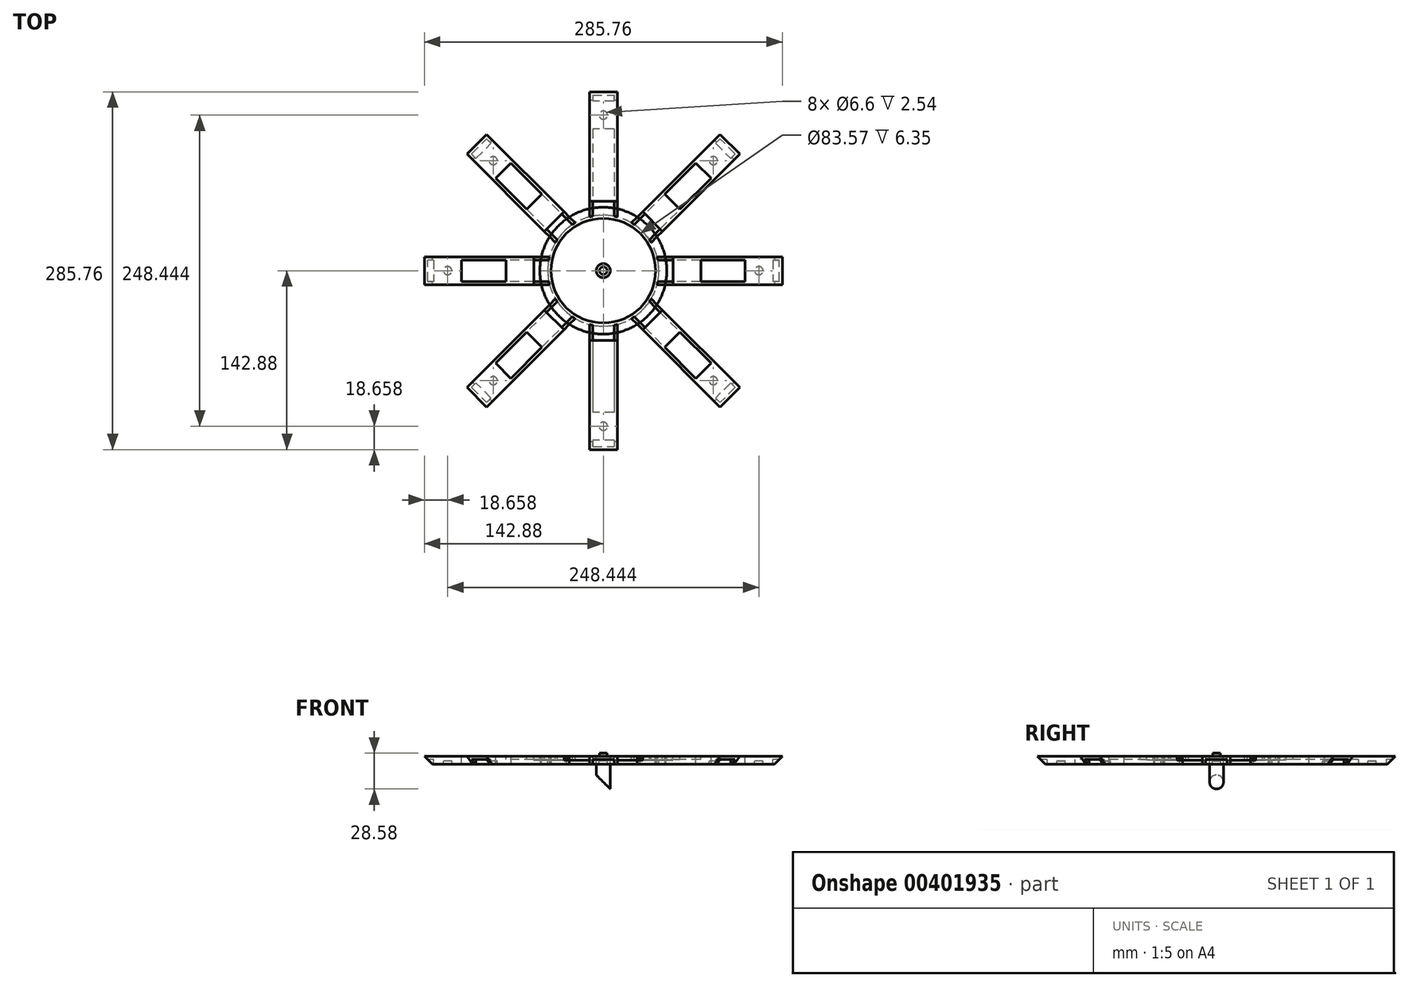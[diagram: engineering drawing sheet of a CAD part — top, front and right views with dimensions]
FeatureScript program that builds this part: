
annotation { "Feature Type Name" : "Feature", "Feature Type Description" : "" }
export const myFeature = defineFeature(function(context is Context, id is Id, definition is map)
    precondition{}
    {
        {
            var Q0;
            Q0=qCreatedBy(makeId("Top.planeOp"),FACE);
            var sketch = newSketch(context, id + "F0", { "sketchPlane" : qUnion([Q0])});
            skCircle(sketch, "E0", {"center": v(0, 0) * mm, "radius": 41.28 * mm, "construction": true});
            skLineSegment(sketch, "E1", {"start": v(0, 0) * mm, "end": v(142.88, 0) * mm, "construction": true});
            skLineSegment(sketch, "E2", {"start": v(0, 0) * mm, "end": v(0, 142.88) * mm, "construction": true});
            skLineSegment(sketch, "E3", {"start": v(0, 0) * mm, "end": v(-142.88, 0) * mm, "construction": true});
            skLineSegment(sketch, "E4", {"start": v(0, 0) * mm, "end": v(0, -142.88) * mm, "construction": true});
            skLineSegment(sketch, "E5", {"start": v(0, 0) * mm, "end": v(101.03, 101.03) * mm, "construction": true});
            skLineSegment(sketch, "E6", {"start": v(0, 0) * mm, "end": v(101.03, -101.03) * mm, "construction": true});
            skLineSegment(sketch, "E7", {"start": v(0, 0) * mm, "end": v(-101.03, -101.03) * mm, "construction": true});
            skLineSegment(sketch, "E8", {"start": v(0, 0) * mm, "end": v(-101.03, 101.03) * mm, "construction": true});
            skLineSegment(sketch, "E9.bottom", {"start": v(-11.11, 142.88) * mm, "end": v(11.11, 142.88) * mm});
            skLineSegment(sketch, "E9.top", {"start": v(-11.11, -142.88) * mm, "end": v(11.11, -142.88) * mm});
            skLineSegment(sketch, "E9.left", {"start": v(-11.11, 142.88) * mm, "end": v(-11.11, -142.88) * mm});
            skLineSegment(sketch, "E9.right", {"start": v(11.11, 142.88) * mm, "end": v(11.11, -142.88) * mm});
            skLineSegment(sketch, "E10.bottom", {"start": v(142.88, -11.11) * mm, "end": v(-142.88, -11.11) * mm});
            skLineSegment(sketch, "E10.top", {"start": v(142.88, 11.11) * mm, "end": v(-142.88, 11.11) * mm});
            skLineSegment(sketch, "E10.left", {"start": v(142.88, -11.11) * mm, "end": v(142.88, 11.11) * mm});
            skLineSegment(sketch, "E10.right", {"start": v(-142.88, -11.11) * mm, "end": v(-142.88, 11.11) * mm});
            skLineSegment(sketch, "E11", {"start": v(-108.89, 93.17) * mm, "end": v(93.17, -108.89) * mm});
            skLineSegment(sketch, "E12", {"start": v(-93.17, 108.89) * mm, "end": v(108.89, -93.17) * mm});
            skLineSegment(sketch, "E13", {"start": v(108.89, -93.17) * mm, "end": v(93.17, -108.89) * mm});
            skLineSegment(sketch, "E14", {"start": v(-108.89, 93.17) * mm, "end": v(-93.17, 108.89) * mm});
            skLineSegment(sketch, "E15", {"start": v(-108.89, -93.17) * mm, "end": v(-93.17, -108.89) * mm});
            skLineSegment(sketch, "E16", {"start": v(-93.17, -108.89) * mm, "end": v(108.89, 93.17) * mm});
            skLineSegment(sketch, "E17", {"start": v(108.89, 93.17) * mm, "end": v(93.17, 108.89) * mm});
            skLineSegment(sketch, "E18", {"start": v(93.17, 108.89) * mm, "end": v(-108.89, -93.17) * mm});
            skLineSegment(sketch, "E19", {"start": v(-120.65, 11.11) * mm, "end": v(-120.65, -11.11) * mm});
            skLineSegment(sketch, "E20", {"start": v(-93.17, 77.45) * mm, "end": v(-77.45, 93.17) * mm});
            skLineSegment(sketch, "E21", {"start": v(-11.11, 120.65) * mm, "end": v(11.11, 120.65) * mm});
            skLineSegment(sketch, "E22", {"start": v(77.45, 93.17) * mm, "end": v(93.17, 77.45) * mm});
            skLineSegment(sketch, "E23", {"start": v(120.65, 11.11) * mm, "end": v(120.65, -11.11) * mm});
            skLineSegment(sketch, "E24", {"start": v(11.11, -120.65) * mm, "end": v(-11.11, -120.65) * mm});
            skLineSegment(sketch, "E25", {"start": v(-93.17, -77.45) * mm, "end": v(-77.45, -93.17) * mm});
            skLineSegment(sketch, "E26", {"start": v(77.45, -93.17) * mm, "end": v(93.17, -77.45) * mm});
            skSolve(sketch);
        }
        {
            var Q0;
            Q0 = qSketchRegion(id + "F0", true);
            extrude(context, id + "F1", {"entities" : qUnion([Q0]), "oppositeDirection" : true, "depth" : 6.35 * mm});
        }
        {
            var Q0;
            Q0=makeQuery(id+"F1.opExtrude","CAP_FACE",FACE,{"disambiguationData":[OSD([sQuery(id+"F0.wireOp",EDGE,"E9.bottom"),sQuery(id+"F0.wireOp",EDGE,"E9.top"),sQuery(id+"F0.wireOp",EDGE,"E9.left"),sQuery(id+"F0.wireOp",EDGE,"E9.right"),sQuery(id+"F0.wireOp",EDGE,"E10.bottom"),sQuery(id+"F0.wireOp",EDGE,"E10.top"),sQuery(id+"F0.wireOp",EDGE,"E10.left"),sQuery(id+"F0.wireOp",EDGE,"E10.right"),sQuery(id+"F0.wireOp",EDGE,"E11"),sQuery(id+"F0.wireOp",EDGE,"E12"),sQuery(id+"F0.wireOp",EDGE,"E13"),sQuery(id+"F0.wireOp",EDGE,"E14"),sQuery(id+"F0.wireOp",EDGE,"E15"),sQuery(id+"F0.wireOp",EDGE,"E16"),sQuery(id+"F0.wireOp",EDGE,"E17"),sQuery(id+"F0.wireOp",EDGE,"E18")])],"isStart":false});
            shell(context, id + "F2", {"entities" : qUnion([Q0]), "thickness" : 2.54 * mm});
        }
        {
            var Q0;
            Q0=makeQuery(id+"F1.opExtrude","CAP_EDGE",EDGE,{"disambiguationData":[OSD([sQuery(id+"F0.wireOp",EDGE,"E15")])],"isStart":false});
            var Q1;
            Q1=makeQuery(id+"F1.opExtrude","CAP_EDGE",EDGE,{"disambiguationData":[OSD([sQuery(id+"F0.wireOp",EDGE,"E10.right")])],"isStart":false});
            var Q2;
            Q2=makeQuery(id+"F1.opExtrude","CAP_EDGE",EDGE,{"disambiguationData":[OSD([sQuery(id+"F0.wireOp",EDGE,"E14")])],"isStart":false});
            var Q3;
            Q3=makeQuery(id+"F1.opExtrude","CAP_EDGE",EDGE,{"disambiguationData":[OSD([sQuery(id+"F0.wireOp",EDGE,"E9.bottom")])],"isStart":false});
            var Q4;
            Q4=makeQuery(id+"F1.opExtrude","CAP_EDGE",EDGE,{"disambiguationData":[OSD([sQuery(id+"F0.wireOp",EDGE,"E17")])],"isStart":false});
            var Q5;
            Q5=makeQuery(id+"F1.opExtrude","CAP_EDGE",EDGE,{"disambiguationData":[OSD([sQuery(id+"F0.wireOp",EDGE,"E10.left")])],"isStart":false});
            var Q6;
            Q6=makeQuery(id+"F1.opExtrude","CAP_EDGE",EDGE,{"disambiguationData":[OSD([sQuery(id+"F0.wireOp",EDGE,"E13")])],"isStart":false});
            var Q7;
            Q7=makeQuery(id+"F1.opExtrude","CAP_EDGE",EDGE,{"disambiguationData":[OSD([sQuery(id+"F0.wireOp",EDGE,"E9.top")])],"isStart":false});
            chamfer(context, id + "F3", {"entities" : qUnion([Q0, Q1, Q2, Q3, Q4, Q5, Q6, Q7]), "width" : 6.35 * mm, "tangentPropagation" : true});
        }
        {
            var Q0;
            Q0=qCreatedBy(makeId("Top.planeOp"),FACE);
            var sketch = newSketch(context, id + "F4", { "sketchPlane" : qUnion([Q0])});
            skLineSegment(sketch, "E27", {"start": v(0, 0) * mm, "end": v(142.88, 0) * mm, "construction": true});
            skLineSegment(sketch, "E28", {"start": v(0, 0) * mm, "end": v(101.03, -101.03) * mm, "construction": true});
            skLineSegment(sketch, "E29", {"start": v(0, 0) * mm, "end": v(0, 142.88) * mm, "construction": true});
            skLineSegment(sketch, "E30", {"start": v(0, 0) * mm, "end": v(101.03, 101.03) * mm, "construction": true});
            skLineSegment(sketch, "E31", {"start": v(0, 0) * mm, "end": v(-101.03, 101.03) * mm, "construction": true});
            skLineSegment(sketch, "E32", {"start": v(0, 0) * mm, "end": v(-101.03, -101.03) * mm, "construction": true});
            skLineSegment(sketch, "E33", {"start": v(0, 0) * mm, "end": v(-142.88, 0) * mm, "construction": true});
            skLineSegment(sketch, "E34", {"start": v(0, 0) * mm, "end": v(0, -142.88) * mm, "construction": true});
            skLineSegment(sketch, "E35", {"start": v(-142.88, 11.11) * mm, "end": v(-142.88, -11.11) * mm});
            skLineSegment(sketch, "E36", {"start": v(-142.88, -11.11) * mm, "end": v(-120.65, -11.11) * mm});
            skLineSegment(sketch, "E37", {"start": v(-120.65, -11.11) * mm, "end": v(-120.65, 11.11) * mm});
            skLineSegment(sketch, "E38", {"start": v(-120.65, 11.11) * mm, "end": v(-142.88, 11.11) * mm});
            skLineSegment(sketch, "E39", {"start": v(142.88, 11.11) * mm, "end": v(142.88, -11.11) * mm});
            skLineSegment(sketch, "E40", {"start": v(142.88, -11.11) * mm, "end": v(120.65, -11.11) * mm});
            skLineSegment(sketch, "E41", {"start": v(120.65, -11.11) * mm, "end": v(120.65, 11.11) * mm});
            skLineSegment(sketch, "E42", {"start": v(120.65, 11.11) * mm, "end": v(142.88, 11.11) * mm});
            skLineSegment(sketch, "E43", {"start": v(11.11, 142.88) * mm, "end": v(-11.11, 142.88) * mm});
            skLineSegment(sketch, "E44", {"start": v(-11.11, 142.88) * mm, "end": v(-11.11, 120.65) * mm});
            skLineSegment(sketch, "E45", {"start": v(-11.11, 120.65) * mm, "end": v(11.11, 120.65) * mm});
            skLineSegment(sketch, "E46", {"start": v(11.11, 120.65) * mm, "end": v(11.11, 142.88) * mm});
            skLineSegment(sketch, "E47", {"start": v(11.11, -142.88) * mm, "end": v(-11.11, -142.88) * mm});
            skLineSegment(sketch, "E48", {"start": v(-11.11, -142.88) * mm, "end": v(-11.11, -120.65) * mm});
            skLineSegment(sketch, "E49", {"start": v(-11.11, -120.65) * mm, "end": v(11.11, -120.65) * mm});
            skLineSegment(sketch, "E50", {"start": v(11.11, -120.65) * mm, "end": v(11.11, -142.88) * mm});
            skLineSegment(sketch, "E51", {"start": v(-101.03, 101.03) * mm, "end": v(-93.17, 108.89) * mm});
            skLineSegment(sketch, "E52", {"start": v(-93.17, 108.89) * mm, "end": v(-77.45, 93.17) * mm});
            skLineSegment(sketch, "E53", {"start": v(-77.45, 93.17) * mm, "end": v(-93.17, 77.45) * mm});
            skLineSegment(sketch, "E54", {"start": v(-93.17, 77.45) * mm, "end": v(-108.89, 93.17) * mm});
            skLineSegment(sketch, "E55", {"start": v(-108.89, 93.17) * mm, "end": v(-101.03, 101.03) * mm});
            skLineSegment(sketch, "E56", {"start": v(101.03, -101.03) * mm, "end": v(108.89, -93.17) * mm});
            skLineSegment(sketch, "E57", {"start": v(108.89, -93.17) * mm, "end": v(93.17, -77.45) * mm});
            skLineSegment(sketch, "E58", {"start": v(93.17, -77.45) * mm, "end": v(77.45, -93.17) * mm});
            skLineSegment(sketch, "E59", {"start": v(77.45, -93.17) * mm, "end": v(93.17, -108.89) * mm});
            skLineSegment(sketch, "E60", {"start": v(93.17, -108.89) * mm, "end": v(101.03, -101.03) * mm});
            skLineSegment(sketch, "E61", {"start": v(101.03, 101.03) * mm, "end": v(93.17, 108.89) * mm});
            skLineSegment(sketch, "E62", {"start": v(93.17, 108.89) * mm, "end": v(77.45, 93.17) * mm});
            skLineSegment(sketch, "E63", {"start": v(77.45, 93.17) * mm, "end": v(93.17, 77.45) * mm});
            skLineSegment(sketch, "E64", {"start": v(93.17, 77.45) * mm, "end": v(108.89, 93.17) * mm});
            skLineSegment(sketch, "E65", {"start": v(108.89, 93.17) * mm, "end": v(101.03, 101.03) * mm});
            skLineSegment(sketch, "E66", {"start": v(-101.03, -101.03) * mm, "end": v(-108.89, -93.17) * mm});
            skLineSegment(sketch, "E67", {"start": v(-108.89, -93.17) * mm, "end": v(-93.17, -77.45) * mm});
            skLineSegment(sketch, "E68", {"start": v(-93.17, -77.45) * mm, "end": v(-77.45, -93.17) * mm});
            skLineSegment(sketch, "E69", {"start": v(-77.45, -93.17) * mm, "end": v(-93.17, -108.89) * mm});
            skLineSegment(sketch, "E70", {"start": v(-93.17, -108.89) * mm, "end": v(-101.03, -101.03) * mm});
            skLineSegment(sketch, "E71", {"start": v(0, 0) * mm, "end": v(0, 77.79) * mm, "construction": true});
            skLineSegment(sketch, "E72", {"start": v(0, 0) * mm, "end": v(55, 55) * mm, "construction": true});
            skLineSegment(sketch, "E73", {"start": v(0, 0) * mm, "end": v(77.79, 0) * mm, "construction": true});
            skLineSegment(sketch, "E74", {"start": v(0, 0) * mm, "end": v(55, -55) * mm, "construction": true});
            skLineSegment(sketch, "E75", {"start": v(0, 0) * mm, "end": v(0, -77.79) * mm, "construction": true});
            skLineSegment(sketch, "E76", {"start": v(0, 0) * mm, "end": v(-55, -55) * mm, "construction": true});
            skLineSegment(sketch, "E77", {"start": v(0, 0) * mm, "end": v(-77.79, 0) * mm, "construction": true});
            skLineSegment(sketch, "E78", {"start": v(0, 0) * mm, "end": v(-55, 55) * mm, "construction": true});
            skLineSegment(sketch, "E79", {"start": v(77.79, 11.11) * mm, "end": v(77.79, -11.11) * mm});
            skLineSegment(sketch, "E80", {"start": v(77.79, -11.11) * mm, "end": v(55.56, -11.11) * mm});
            skLineSegment(sketch, "E81", {"start": v(55.56, -11.11) * mm, "end": v(55.56, 11.11) * mm});
            skLineSegment(sketch, "E82", {"start": v(55.56, 11.11) * mm, "end": v(77.79, 11.11) * mm});
            skLineSegment(sketch, "E83", {"start": v(55, -55) * mm, "end": v(47.15, -62.86) * mm});
            skLineSegment(sketch, "E84", {"start": v(47.15, -62.86) * mm, "end": v(31.43, -47.15) * mm});
            skLineSegment(sketch, "E85", {"start": v(31.43, -47.15) * mm, "end": v(47.15, -31.43) * mm});
            skLineSegment(sketch, "E86", {"start": v(47.15, -31.43) * mm, "end": v(62.86, -47.15) * mm});
            skLineSegment(sketch, "E87", {"start": v(62.86, -47.15) * mm, "end": v(55, -55) * mm});
            skLineSegment(sketch, "E88", {"start": v(11.11, -77.79) * mm, "end": v(-11.11, -77.79) * mm});
            skLineSegment(sketch, "E89", {"start": v(-11.11, -77.79) * mm, "end": v(-11.11, -55.56) * mm});
            skLineSegment(sketch, "E90", {"start": v(-11.11, -55.56) * mm, "end": v(11.11, -55.56) * mm});
            skLineSegment(sketch, "E91", {"start": v(11.11, -55.56) * mm, "end": v(11.11, -77.79) * mm});
            skLineSegment(sketch, "E92", {"start": v(-55, -55) * mm, "end": v(-62.86, -47.15) * mm});
            skLineSegment(sketch, "E93", {"start": v(-62.86, -47.15) * mm, "end": v(-47.15, -31.43) * mm});
            skLineSegment(sketch, "E94", {"start": v(-47.15, -31.43) * mm, "end": v(-31.43, -47.15) * mm});
            skLineSegment(sketch, "E95", {"start": v(-31.43, -47.15) * mm, "end": v(-47.15, -62.86) * mm});
            skLineSegment(sketch, "E96", {"start": v(-47.15, -62.86) * mm, "end": v(-55, -55) * mm});
            skLineSegment(sketch, "E97", {"start": v(-77.79, 11.11) * mm, "end": v(-77.79, -11.11) * mm});
            skLineSegment(sketch, "E98", {"start": v(-77.79, -11.11) * mm, "end": v(-55.56, -11.11) * mm});
            skLineSegment(sketch, "E99", {"start": v(-55.56, -11.11) * mm, "end": v(-55.56, 11.11) * mm});
            skLineSegment(sketch, "E100", {"start": v(-55.56, 11.11) * mm, "end": v(-77.79, 11.11) * mm});
            skLineSegment(sketch, "E101", {"start": v(-55, 55) * mm, "end": v(-47.15, 62.86) * mm});
            skLineSegment(sketch, "E102", {"start": v(-47.15, 62.86) * mm, "end": v(-31.43, 47.15) * mm});
            skLineSegment(sketch, "E103", {"start": v(-31.43, 47.15) * mm, "end": v(-47.15, 31.43) * mm});
            skLineSegment(sketch, "E104", {"start": v(-47.15, 31.43) * mm, "end": v(-62.86, 47.15) * mm});
            skLineSegment(sketch, "E105", {"start": v(-62.86, 47.15) * mm, "end": v(-55, 55) * mm});
            skLineSegment(sketch, "E106", {"start": v(-11.11, 77.79) * mm, "end": v(11.11, 77.79) * mm});
            skLineSegment(sketch, "E107", {"start": v(11.11, 77.79) * mm, "end": v(11.11, 55.56) * mm});
            skLineSegment(sketch, "E108", {"start": v(11.11, 55.56) * mm, "end": v(-11.11, 55.56) * mm});
            skLineSegment(sketch, "E109", {"start": v(-11.11, 55.56) * mm, "end": v(-11.11, 77.79) * mm});
            skLineSegment(sketch, "E110", {"start": v(55, 55) * mm, "end": v(62.86, 47.15) * mm});
            skLineSegment(sketch, "E111", {"start": v(62.86, 47.15) * mm, "end": v(47.15, 31.43) * mm});
            skLineSegment(sketch, "E112", {"start": v(47.15, 31.43) * mm, "end": v(31.43, 47.15) * mm});
            skLineSegment(sketch, "E113", {"start": v(31.43, 47.15) * mm, "end": v(47.15, 62.86) * mm});
            skLineSegment(sketch, "E114", {"start": v(47.15, 62.86) * mm, "end": v(55, 55) * mm});
            skLineSegment(sketch, "E115", {"start": v(0, 77.79) * mm, "end": v(0, 120.65) * mm, "construction": true});
            skLineSegment(sketch, "E116", {"start": v(55, 55) * mm, "end": v(85.31, 85.31) * mm, "construction": true});
            skLineSegment(sketch, "E117", {"start": v(77.79, 0) * mm, "end": v(120.65, 0) * mm, "construction": true});
            skLineSegment(sketch, "E118", {"start": v(55, -55) * mm, "end": v(85.31, -85.31) * mm, "construction": true});
            skLineSegment(sketch, "E119", {"start": v(0, -77.79) * mm, "end": v(0, -120.65) * mm, "construction": true});
            skLineSegment(sketch, "E120", {"start": v(-55, -55) * mm, "end": v(-85.31, -85.31) * mm, "construction": true});
            skLineSegment(sketch, "E121", {"start": v(-77.79, 0) * mm, "end": v(-120.65, 0) * mm, "construction": true});
            skLineSegment(sketch, "E122", {"start": v(-55, 55) * mm, "end": v(-85.31, 85.31) * mm, "construction": true});
            skLineSegment(sketch, "E123.bottom", {"start": v(8.57, 77.79) * mm, "end": v(-8.57, 77.79) * mm});
            skLineSegment(sketch, "E123.top", {"start": v(8.57, 120.65) * mm, "end": v(-8.57, 120.65) * mm});
            skLineSegment(sketch, "E123.left", {"start": v(8.57, 77.79) * mm, "end": v(8.57, 120.65) * mm});
            skLineSegment(sketch, "E123.right", {"start": v(-8.57, 77.79) * mm, "end": v(-8.57, 120.65) * mm});
            skPoint(sketch, "E123.middle", {"position": v(0, 99.22) * mm});
            skLineSegment(sketch, "E124.bottom", {"start": v(77.79, 8.57) * mm, "end": v(120.65, 8.57) * mm});
            skLineSegment(sketch, "E124.top", {"start": v(77.79, -8.57) * mm, "end": v(120.65, -8.57) * mm});
            skLineSegment(sketch, "E124.left", {"start": v(77.79, 8.57) * mm, "end": v(77.79, -8.57) * mm});
            skLineSegment(sketch, "E124.right", {"start": v(120.65, 8.57) * mm, "end": v(120.65, -8.57) * mm});
            skPoint(sketch, "E124.middle", {"position": v(99.22, 0) * mm});
            skLineSegment(sketch, "E125.bottom", {"start": v(8.57, -77.79) * mm, "end": v(-8.57, -77.79) * mm});
            skLineSegment(sketch, "E125.top", {"start": v(8.57, -120.65) * mm, "end": v(-8.57, -120.65) * mm});
            skLineSegment(sketch, "E125.left", {"start": v(8.57, -77.79) * mm, "end": v(8.57, -120.65) * mm});
            skLineSegment(sketch, "E125.right", {"start": v(-8.57, -77.79) * mm, "end": v(-8.57, -120.65) * mm});
            skPoint(sketch, "E125.middle", {"position": v(0, -99.22) * mm});
            skLineSegment(sketch, "E126.bottom", {"start": v(-77.79, -8.57) * mm, "end": v(-120.65, -8.57) * mm});
            skLineSegment(sketch, "E126.top", {"start": v(-77.79, 8.57) * mm, "end": v(-120.65, 8.57) * mm});
            skLineSegment(sketch, "E126.left", {"start": v(-77.79, -8.57) * mm, "end": v(-77.79, 8.57) * mm});
            skLineSegment(sketch, "E126.right", {"start": v(-120.65, -8.57) * mm, "end": v(-120.65, 8.57) * mm});
            skPoint(sketch, "E126.middle", {"position": v(-99.22, 0) * mm});
            skLineSegment(sketch, "E127", {"start": v(-79.25, 91.37) * mm, "end": v(-48.94, 61.07) * mm});
            skLineSegment(sketch, "E128", {"start": v(-91.37, 79.25) * mm, "end": v(-61.07, 48.94) * mm});
            skLineSegment(sketch, "E129", {"start": v(79.25, 91.37) * mm, "end": v(48.94, 61.07) * mm});
            skLineSegment(sketch, "E130", {"start": v(91.37, 79.25) * mm, "end": v(61.07, 48.94) * mm});
            skLineSegment(sketch, "E131", {"start": v(-91.37, -79.25) * mm, "end": v(-61.07, -48.94) * mm});
            skLineSegment(sketch, "E132", {"start": v(-79.25, -91.37) * mm, "end": v(-48.94, -61.07) * mm});
            skLineSegment(sketch, "E133", {"start": v(48.94, -61.07) * mm, "end": v(79.25, -91.37) * mm});
            skLineSegment(sketch, "E134", {"start": v(61.07, -48.94) * mm, "end": v(91.37, -79.25) * mm});
            skLineSegment(sketch, "E135", {"start": v(-77.79, 8.57) * mm, "end": v(77.79, 8.57) * mm});
            skLineSegment(sketch, "E136", {"start": v(-77.79, -8.57) * mm, "end": v(77.79, -8.57) * mm});
            skLineSegment(sketch, "E137", {"start": v(-8.57, 77.79) * mm, "end": v(-8.57, -77.79) * mm});
            skLineSegment(sketch, "E138", {"start": v(8.57, 77.79) * mm, "end": v(8.57, -77.79) * mm});
            skLineSegment(sketch, "E139", {"start": v(-61.07, 48.94) * mm, "end": v(48.94, -61.07) * mm});
            skLineSegment(sketch, "E140", {"start": v(-48.94, 61.07) * mm, "end": v(61.07, -48.94) * mm});
            skLineSegment(sketch, "E141", {"start": v(-61.07, -48.94) * mm, "end": v(48.94, 61.07) * mm});
            skLineSegment(sketch, "E142", {"start": v(-48.94, -61.07) * mm, "end": v(61.07, 48.94) * mm});
            skLineSegment(sketch, "E143", {"start": v(-31.43, 47.15) * mm, "end": v(47.15, -31.43) * mm});
            skLineSegment(sketch, "E144", {"start": v(-47.15, 31.43) * mm, "end": v(31.43, -47.15) * mm});
            skLineSegment(sketch, "E145", {"start": v(-11.11, 55.56) * mm, "end": v(-11.11, -55.56) * mm});
            skLineSegment(sketch, "E146", {"start": v(11.11, 55.56) * mm, "end": v(11.11, -55.56) * mm});
            skLineSegment(sketch, "E147", {"start": v(31.43, 47.15) * mm, "end": v(-47.15, -31.43) * mm});
            skLineSegment(sketch, "E148", {"start": v(-31.43, -47.15) * mm, "end": v(47.15, 31.43) * mm});
            skLineSegment(sketch, "E149", {"start": v(55.56, 11.11) * mm, "end": v(-55.56, 11.11) * mm});
            skLineSegment(sketch, "E150", {"start": v(-55.56, -11.11) * mm, "end": v(55.56, -11.11) * mm});
            skCircle(sketch, "E151", {"center": v(0, 0) * mm, "radius": 44.32 * mm});
            skSolve(sketch);
        }
        {
            var Q0;
            Q0=makeQuery(id+"F4.imprint","IMPRINT",FACE,{"disambiguationData":[TD([[makeQuery(id+"F4.imprint","IMPRINT",EDGE,{"derivedFrom":sQuery(id+"F4.wireOp",EDGE,"E126.bottom")}),-1.0]])]});
            var Q1;
            {var subQ4=sQuery(id+"F4.wireOp",EDGE,"E127");Q1=makeQuery(id+"F4.imprint","IMPRINT",FACE,{"disambiguationData":[TD([[makeQuery(id+"F4.imprint","IMPRINT",EDGE,{"derivedFrom":subQ4}),-1.0]])]});}
            var Q2;
            Q2=makeQuery(id+"F4.imprint","IMPRINT",FACE,{"disambiguationData":[TD([[makeQuery(id+"F4.imprint","IMPRINT",EDGE,{"derivedFrom":sQuery(id+"F4.wireOp",EDGE,"E123.bottom")}),-1.0]])]});
            var Q3;
            {var subQ0=sQuery(id+"F4.wireOp",EDGE,"E129");Q3=makeQuery(id+"F4.imprint","IMPRINT",FACE,{"disambiguationData":[TD([[makeQuery(id+"F4.imprint","IMPRINT",EDGE,{"derivedFrom":subQ0}),1.0]])]});}
            var Q4;
            Q4=makeQuery(id+"F4.imprint","IMPRINT",FACE,{"disambiguationData":[TD([[makeQuery(id+"F4.imprint","IMPRINT",EDGE,{"derivedFrom":sQuery(id+"F4.wireOp",EDGE,"E124.bottom")}),-1.0]])]});
            var Q5;
            {var subQ0=sQuery(id+"F4.wireOp",EDGE,"E133");Q5=makeQuery(id+"F4.imprint","IMPRINT",FACE,{"disambiguationData":[TD([[makeQuery(id+"F4.imprint","IMPRINT",EDGE,{"derivedFrom":subQ0}),1.0]])]});}
            var Q6;
            Q6=makeQuery(id+"F4.imprint","IMPRINT",FACE,{"disambiguationData":[TD([[makeQuery(id+"F4.imprint","IMPRINT",EDGE,{"derivedFrom":sQuery(id+"F4.wireOp",EDGE,"E125.bottom")}),1.0]])]});
            var Q7;
            {var subQ0=sQuery(id+"F4.wireOp",EDGE,"E131");Q7=makeQuery(id+"F4.imprint","IMPRINT",FACE,{"disambiguationData":[TD([[makeQuery(id+"F4.imprint","IMPRINT",EDGE,{"derivedFrom":subQ0}),-1.0]])]});}
            extrude(context, id + "F5", {"entities" : qUnion([Q0, Q1, Q2, Q3, Q4, Q5, Q6, Q7]), "operationType" : NewBodyOperationType.REMOVE, "oppositeDirection" : true, "depth" : 25.4 * mm});
        }
        {
            var Q0;
            {var subQ1=sQuery(id+"F4.wireOp",EDGE,"E103");var subQ7=sQuery(id+"F4.wireOp",EDGE,"E140");var subQ8=makeQuery(id+"F4.imprint","INTERSECT",VERTEX,{"derivedFrom":[subQ1,subQ7]});Q0=makeQuery(id+"F4.imprint","IMPRINT",FACE,{"disambiguationData":[TD([[makeQuery(id+"F4.imprint","IMPRINT",EDGE,{"disambiguationData":[TD([[subQ8,-1.0]])],"derivedFrom":subQ1}),1.0]])]});}
            var Q1;
            {var subQ0=sQuery(id+"F4.wireOp",EDGE,"E139");var subQ1=sQuery(id+"F4.wireOp",EDGE,"E135");var subQ2=makeQuery(id+"F4.imprint","INTERSECT",VERTEX,{"derivedFrom":[subQ1,subQ0]});Q1=makeQuery(id+"F4.imprint","IMPRINT",FACE,{"disambiguationData":[TD([[makeQuery(id+"F4.imprint","IMPRINT",EDGE,{"disambiguationData":[TD([[subQ2,-1.0]])],"derivedFrom":subQ1}),1.0]])]});}
            var Q2;
            {var subQ0=sQuery(id+"F4.wireOp",EDGE,"E140");var subQ1=sQuery(id+"F4.wireOp",EDGE,"E137");var subQ2=makeQuery(id+"F4.imprint","INTERSECT",VERTEX,{"derivedFrom":[subQ1,subQ0]});Q2=makeQuery(id+"F4.imprint","IMPRINT",FACE,{"disambiguationData":[TD([[makeQuery(id+"F4.imprint","IMPRINT",EDGE,{"disambiguationData":[TD([[subQ2,-1.0]])],"derivedFrom":subQ1}),-1.0]])]});}
            var Q3;
            {var subQ5=sQuery(id+"F4.wireOp",EDGE,"E138");var subQ6=sQuery(id+"F4.wireOp",EDGE,"E108");var subQ7=makeQuery(id+"F4.imprint","INTERSECT",VERTEX,{"derivedFrom":[subQ6,subQ5]});Q3=makeQuery(id+"F4.imprint","IMPRINT",FACE,{"disambiguationData":[TD([[makeQuery(id+"F4.imprint","IMPRINT",EDGE,{"disambiguationData":[TD([[subQ7,-1.0]])],"derivedFrom":subQ6}),1.0]])]});}
            var Q4;
            {var subQ0=sQuery(id+"F4.wireOp",EDGE,"E143");var subQ1=sQuery(id+"F4.wireOp",EDGE,"E137");var subQ2=makeQuery(id+"F4.imprint","INTERSECT",VERTEX,{"derivedFrom":[subQ1,subQ0]});Q4=makeQuery(id+"F4.imprint","IMPRINT",FACE,{"disambiguationData":[TD([[makeQuery(id+"F4.imprint","IMPRINT",EDGE,{"disambiguationData":[TD([[subQ2,-1.0]])],"derivedFrom":subQ1}),1.0]])]});}
            var Q5;
            {var subQ0=sQuery(id+"F4.wireOp",EDGE,"E147");var subQ1=sQuery(id+"F4.wireOp",EDGE,"E138");var subQ2=makeQuery(id+"F4.imprint","INTERSECT",VERTEX,{"derivedFrom":[subQ1,subQ0]});Q5=makeQuery(id+"F4.imprint","IMPRINT",FACE,{"disambiguationData":[TD([[makeQuery(id+"F4.imprint","IMPRINT",EDGE,{"disambiguationData":[TD([[subQ2,-1.0]])],"derivedFrom":subQ1}),-1.0]])]});}
            var Q6;
            {var subQ0=sQuery(id+"F4.wireOp",EDGE,"E142");var subQ1=sQuery(id+"F4.wireOp",EDGE,"E112");var subQ2=makeQuery(id+"F4.imprint","INTERSECT",VERTEX,{"derivedFrom":[subQ1,subQ0]});Q6=makeQuery(id+"F4.imprint","IMPRINT",FACE,{"disambiguationData":[TD([[makeQuery(id+"F4.imprint","IMPRINT",EDGE,{"disambiguationData":[TD([[subQ2,-1.0]])],"derivedFrom":subQ1}),1.0]])]});}
            var Q7;
            {var subQ0=sQuery(id+"F4.wireOp",EDGE,"E141");var subQ1=sQuery(id+"F4.wireOp",EDGE,"E138");var subQ2=makeQuery(id+"F4.imprint","INTERSECT",VERTEX,{"derivedFrom":[subQ1,subQ0]});Q7=makeQuery(id+"F4.imprint","IMPRINT",FACE,{"disambiguationData":[TD([[makeQuery(id+"F4.imprint","IMPRINT",EDGE,{"disambiguationData":[TD([[subQ2,-1.0]])],"derivedFrom":subQ1}),1.0]])]});}
            var Q8;
            {var subQ0=sQuery(id+"F4.wireOp",EDGE,"E146");var subQ1=sQuery(id+"F4.wireOp",EDGE,"E135");var subQ2=makeQuery(id+"F4.imprint","INTERSECT",VERTEX,{"derivedFrom":[subQ1,subQ0]});Q8=makeQuery(id+"F4.imprint","IMPRINT",FACE,{"disambiguationData":[TD([[makeQuery(id+"F4.imprint","IMPRINT",EDGE,{"disambiguationData":[TD([[subQ2,-1.0]])],"derivedFrom":subQ1}),1.0]])]});}
            var Q9;
            {var subQ1=sQuery(id+"F4.wireOp",EDGE,"E136");var subQ5=sQuery(id+"F4.wireOp",EDGE,"E81");var subQ6=makeQuery(id+"F4.imprint","INTERSECT",VERTEX,{"derivedFrom":[subQ5,subQ1]});Q9=makeQuery(id+"F4.imprint","IMPRINT",FACE,{"disambiguationData":[TD([[makeQuery(id+"F4.imprint","IMPRINT",EDGE,{"disambiguationData":[TD([[subQ6,-1.0]])],"derivedFrom":subQ5}),1.0]])]});}
            var Q10;
            {var subQ0=sQuery(id+"F4.wireOp",EDGE,"E142");var subQ1=sQuery(id+"F4.wireOp",EDGE,"E135");var subQ2=makeQuery(id+"F4.imprint","INTERSECT",VERTEX,{"derivedFrom":[subQ1,subQ0]});Q10=makeQuery(id+"F4.imprint","IMPRINT",FACE,{"disambiguationData":[TD([[makeQuery(id+"F4.imprint","IMPRINT",EDGE,{"disambiguationData":[TD([[subQ2,-1.0]])],"derivedFrom":subQ1}),-1.0]])]});}
            var Q11;
            {var subQ0=sQuery(id+"F4.wireOp",EDGE,"E140");var subQ1=sQuery(id+"F4.wireOp",EDGE,"E136");var subQ2=makeQuery(id+"F4.imprint","INTERSECT",VERTEX,{"derivedFrom":[subQ1,subQ0]});Q11=makeQuery(id+"F4.imprint","IMPRINT",FACE,{"disambiguationData":[TD([[makeQuery(id+"F4.imprint","IMPRINT",EDGE,{"disambiguationData":[TD([[subQ2,-1.0]])],"derivedFrom":subQ1}),1.0]])]});}
            var Q12;
            {var subQ1=sQuery(id+"F4.wireOp",EDGE,"E139");var subQ6=sQuery(id+"F4.wireOp",EDGE,"E85");var subQ9=makeQuery(id+"F4.imprint","INTERSECT",VERTEX,{"derivedFrom":[subQ6,subQ1]});Q12=makeQuery(id+"F4.imprint","IMPRINT",FACE,{"disambiguationData":[TD([[makeQuery(id+"F4.imprint","IMPRINT",EDGE,{"disambiguationData":[TD([[subQ9,-1.0]])],"derivedFrom":subQ6}),1.0]])]});}
            var Q13;
            {var subQ0=sQuery(id+"F4.wireOp",EDGE,"E146");var subQ1=sQuery(id+"F4.wireOp",EDGE,"E136");var subQ2=makeQuery(id+"F4.imprint","INTERSECT",VERTEX,{"derivedFrom":[subQ1,subQ0]});Q13=makeQuery(id+"F4.imprint","IMPRINT",FACE,{"disambiguationData":[TD([[makeQuery(id+"F4.imprint","IMPRINT",EDGE,{"disambiguationData":[TD([[subQ2,-1.0]])],"derivedFrom":subQ1}),-1.0]])]});}
            var Q14;
            {var subQ0=sQuery(id+"F4.wireOp",EDGE,"E150");var subQ1=sQuery(id+"F4.wireOp",EDGE,"E138");var subQ2=makeQuery(id+"F4.imprint","INTERSECT",VERTEX,{"derivedFrom":[subQ1,subQ0]});Q14=makeQuery(id+"F4.imprint","IMPRINT",FACE,{"disambiguationData":[TD([[makeQuery(id+"F4.imprint","IMPRINT",EDGE,{"disambiguationData":[TD([[subQ2,-1.0]])],"derivedFrom":subQ1}),1.0]])]});}
            var Q15;
            {var subQ5=sQuery(id+"F4.wireOp",EDGE,"E137");var subQ7=sQuery(id+"F4.wireOp",EDGE,"E90");var subQ9=makeQuery(id+"F4.imprint","INTERSECT",VERTEX,{"derivedFrom":[subQ7,subQ5]});Q15=makeQuery(id+"F4.imprint","IMPRINT",FACE,{"disambiguationData":[TD([[makeQuery(id+"F4.imprint","IMPRINT",EDGE,{"disambiguationData":[TD([[subQ9,-1.0]])],"derivedFrom":subQ7}),1.0]])]});}
            var Q16;
            {var subQ0=sQuery(id+"F4.wireOp",EDGE,"E142");var subQ1=sQuery(id+"F4.wireOp",EDGE,"E137");var subQ2=makeQuery(id+"F4.imprint","INTERSECT",VERTEX,{"derivedFrom":[subQ1,subQ0]});Q16=makeQuery(id+"F4.imprint","IMPRINT",FACE,{"disambiguationData":[TD([[makeQuery(id+"F4.imprint","IMPRINT",EDGE,{"disambiguationData":[TD([[subQ2,-1.0]])],"derivedFrom":subQ1}),1.0]])]});}
            var Q17;
            {var subQ0=sQuery(id+"F4.wireOp",EDGE,"E139");var subQ1=sQuery(id+"F4.wireOp",EDGE,"E138");var subQ2=makeQuery(id+"F4.imprint","INTERSECT",VERTEX,{"derivedFrom":[subQ1,subQ0]});Q17=makeQuery(id+"F4.imprint","IMPRINT",FACE,{"disambiguationData":[TD([[makeQuery(id+"F4.imprint","IMPRINT",EDGE,{"disambiguationData":[TD([[subQ2,-1.0]])],"derivedFrom":subQ1}),-1.0]])]});}
            var Q18;
            {var subQ5=sQuery(id+"F4.wireOp",EDGE,"E94");var subQ7=sQuery(id+"F4.wireOp",EDGE,"E141");var subQ8=makeQuery(id+"F4.imprint","INTERSECT",VERTEX,{"derivedFrom":[subQ5,subQ7]});Q18=makeQuery(id+"F4.imprint","IMPRINT",FACE,{"disambiguationData":[TD([[makeQuery(id+"F4.imprint","IMPRINT",EDGE,{"disambiguationData":[TD([[subQ8,-1.0]])],"derivedFrom":subQ5}),1.0]])]});}
            var Q19;
            {var subQ0=sQuery(id+"F4.wireOp",EDGE,"E141");var subQ1=sQuery(id+"F4.wireOp",EDGE,"E136");var subQ2=makeQuery(id+"F4.imprint","INTERSECT",VERTEX,{"derivedFrom":[subQ1,subQ0]});Q19=makeQuery(id+"F4.imprint","IMPRINT",FACE,{"disambiguationData":[TD([[makeQuery(id+"F4.imprint","IMPRINT",EDGE,{"disambiguationData":[TD([[subQ2,-1.0]])],"derivedFrom":subQ1}),-1.0]])]});}
            var Q20;
            {var subQ0=sQuery(id+"F4.wireOp",EDGE,"E150");var subQ1=sQuery(id+"F4.wireOp",EDGE,"E137");var subQ2=makeQuery(id+"F4.imprint","INTERSECT",VERTEX,{"derivedFrom":[subQ1,subQ0]});Q20=makeQuery(id+"F4.imprint","IMPRINT",FACE,{"disambiguationData":[TD([[makeQuery(id+"F4.imprint","IMPRINT",EDGE,{"disambiguationData":[TD([[subQ2,-1.0]])],"derivedFrom":subQ1}),-1.0]])]});}
            var Q21;
            {var subQ5=sQuery(id+"F4.wireOp",EDGE,"E136");var subQ6=sQuery(id+"F4.wireOp",EDGE,"E99");var subQ7=makeQuery(id+"F4.imprint","INTERSECT",VERTEX,{"derivedFrom":[subQ6,subQ5]});Q21=makeQuery(id+"F4.imprint","IMPRINT",FACE,{"disambiguationData":[TD([[makeQuery(id+"F4.imprint","IMPRINT",EDGE,{"disambiguationData":[TD([[subQ7,-1.0]])],"derivedFrom":subQ6}),-1.0]])]});}
            var Q22;
            {var subQ0=sQuery(id+"F4.wireOp",EDGE,"E147");var subQ1=sQuery(id+"F4.wireOp",EDGE,"E136");var subQ2=makeQuery(id+"F4.imprint","INTERSECT",VERTEX,{"derivedFrom":[subQ1,subQ0]});Q22=makeQuery(id+"F4.imprint","IMPRINT",FACE,{"disambiguationData":[TD([[makeQuery(id+"F4.imprint","IMPRINT",EDGE,{"disambiguationData":[TD([[subQ2,-1.0]])],"derivedFrom":subQ1}),1.0]])]});}
            var Q23;
            {var subQ0=sQuery(id+"F4.wireOp",EDGE,"E144");var subQ1=sQuery(id+"F4.wireOp",EDGE,"E135");var subQ2=makeQuery(id+"F4.imprint","INTERSECT",VERTEX,{"derivedFrom":[subQ1,subQ0]});Q23=makeQuery(id+"F4.imprint","IMPRINT",FACE,{"disambiguationData":[TD([[makeQuery(id+"F4.imprint","IMPRINT",EDGE,{"disambiguationData":[TD([[subQ2,-1.0]])],"derivedFrom":subQ1}),-1.0]])]});}
            extrude(context, id + "F6", {"entities" : qUnion([Q0, Q1, Q2, Q3, Q4, Q5, Q6, Q7, Q8, Q9, Q10, Q11, Q12, Q13, Q14, Q15, Q16, Q17, Q18, Q19, Q20, Q21, Q22, Q23]), "operationType" : NewBodyOperationType.REMOVE, "oppositeDirection" : true, "depth" : 25.4 * mm});
        }
        {
            var Q0;
            Q0=qCreatedBy(makeId("Top.planeOp"),FACE);
            var sketch = newSketch(context, id + "F7", { "sketchPlane" : qUnion([Q0])});
            skLineSegment(sketch, "E152", {"start": v(0, 0) * mm, "end": v(124.22, 0) * mm, "construction": true});
            skLineSegment(sketch, "E153", {"start": v(0, 0) * mm, "end": v(87.84, 87.84) * mm, "construction": true});
            skLineSegment(sketch, "E154", {"start": v(0, 0) * mm, "end": v(0, 124.22) * mm, "construction": true});
            skLineSegment(sketch, "E155", {"start": v(0, 0) * mm, "end": v(-87.84, 87.84) * mm, "construction": true});
            skLineSegment(sketch, "E156", {"start": v(0, 0) * mm, "end": v(-124.22, 0) * mm, "construction": true});
            skLineSegment(sketch, "E157", {"start": v(0, 0) * mm, "end": v(-87.84, -87.84) * mm, "construction": true});
            skLineSegment(sketch, "E158", {"start": v(0, 0) * mm, "end": v(0, -124.22) * mm, "construction": true});
            skLineSegment(sketch, "E159", {"start": v(0, 0) * mm, "end": v(87.84, -87.84) * mm, "construction": true});
            skLineSegment(sketch, "E160.bottom", {"start": v(-113.1, 11.11) * mm, "end": v(-135.33, 11.11) * mm});
            skLineSegment(sketch, "E160.top", {"start": v(-113.1, -11.11) * mm, "end": v(-135.33, -11.11) * mm});
            skLineSegment(sketch, "E160.left", {"start": v(-113.1, 11.11) * mm, "end": v(-113.1, -11.11) * mm});
            skLineSegment(sketch, "E160.right", {"start": v(-135.33, 11.11) * mm, "end": v(-135.33, -11.11) * mm});
            skPoint(sketch, "E160.middle", {"position": v(-124.22, 0) * mm});
            skLineSegment(sketch, "E161.bottom", {"start": v(11.11, 113.1) * mm, "end": v(-11.11, 113.1) * mm});
            skLineSegment(sketch, "E161.top", {"start": v(11.11, 135.33) * mm, "end": v(-11.11, 135.33) * mm});
            skLineSegment(sketch, "E161.left", {"start": v(11.11, 113.1) * mm, "end": v(11.11, 135.33) * mm});
            skLineSegment(sketch, "E161.right", {"start": v(-11.11, 113.1) * mm, "end": v(-11.11, 135.33) * mm});
            skPoint(sketch, "E161.middle", {"position": v(0, 124.22) * mm});
            skLineSegment(sketch, "E162.bottom", {"start": v(135.33, 11.11) * mm, "end": v(113.1, 11.11) * mm});
            skLineSegment(sketch, "E162.top", {"start": v(135.33, -11.11) * mm, "end": v(113.1, -11.11) * mm});
            skLineSegment(sketch, "E162.left", {"start": v(135.33, 11.11) * mm, "end": v(135.33, -11.11) * mm});
            skLineSegment(sketch, "E162.right", {"start": v(113.1, 11.11) * mm, "end": v(113.1, -11.11) * mm});
            skPoint(sketch, "E162.middle", {"position": v(124.22, 0) * mm});
            skLineSegment(sketch, "E163.bottom", {"start": v(11.11, -113.1) * mm, "end": v(-11.11, -113.1) * mm});
            skLineSegment(sketch, "E163.top", {"start": v(11.11, -135.33) * mm, "end": v(-11.11, -135.33) * mm});
            skLineSegment(sketch, "E163.left", {"start": v(11.11, -113.1) * mm, "end": v(11.11, -135.33) * mm});
            skLineSegment(sketch, "E163.right", {"start": v(-11.11, -113.1) * mm, "end": v(-11.11, -135.33) * mm});
            skPoint(sketch, "E163.middle", {"position": v(0, -124.22) * mm});
            skLineSegment(sketch, "E164", {"start": v(-103.55, 87.84) * mm, "end": v(-87.84, 103.55) * mm});
            skLineSegment(sketch, "E165", {"start": v(-87.84, 103.55) * mm, "end": v(-72.12, 87.84) * mm});
            skLineSegment(sketch, "E166", {"start": v(-72.12, 87.84) * mm, "end": v(-87.84, 72.12) * mm});
            skLineSegment(sketch, "E167", {"start": v(-87.84, 72.12) * mm, "end": v(-103.55, 87.84) * mm});
            skLineSegment(sketch, "E168", {"start": v(-95.7, 95.7) * mm, "end": v(-87.84, 87.84) * mm});
            skLineSegment(sketch, "E169", {"start": v(87.84, 87.84) * mm, "end": v(95.7, 95.7) * mm});
            skLineSegment(sketch, "E170", {"start": v(95.7, 95.7) * mm, "end": v(103.55, 87.84) * mm});
            skLineSegment(sketch, "E171", {"start": v(103.55, 87.84) * mm, "end": v(87.84, 72.12) * mm});
            skLineSegment(sketch, "E172", {"start": v(87.84, 72.12) * mm, "end": v(72.12, 87.84) * mm});
            skLineSegment(sketch, "E173", {"start": v(72.12, 87.84) * mm, "end": v(87.84, 103.55) * mm});
            skLineSegment(sketch, "E174", {"start": v(87.84, 103.55) * mm, "end": v(95.7, 95.7) * mm});
            skLineSegment(sketch, "E175", {"start": v(87.84, -87.84) * mm, "end": v(95.7, -95.7) * mm});
            skLineSegment(sketch, "E176", {"start": v(95.7, -95.7) * mm, "end": v(87.84, -103.55) * mm});
            skLineSegment(sketch, "E177", {"start": v(87.84, -103.55) * mm, "end": v(72.12, -87.84) * mm});
            skLineSegment(sketch, "E178", {"start": v(72.12, -87.84) * mm, "end": v(87.84, -72.12) * mm});
            skLineSegment(sketch, "E179", {"start": v(87.84, -72.12) * mm, "end": v(103.55, -87.84) * mm});
            skLineSegment(sketch, "E180", {"start": v(103.55, -87.84) * mm, "end": v(95.7, -95.7) * mm});
            skLineSegment(sketch, "E181", {"start": v(-87.84, -87.84) * mm, "end": v(-95.7, -95.7) * mm});
            skLineSegment(sketch, "E182", {"start": v(-95.7, -95.7) * mm, "end": v(-103.55, -87.84) * mm});
            skLineSegment(sketch, "E183", {"start": v(-103.55, -87.84) * mm, "end": v(-87.84, -72.12) * mm});
            skLineSegment(sketch, "E184", {"start": v(-87.84, -72.12) * mm, "end": v(-72.12, -87.84) * mm});
            skLineSegment(sketch, "E185", {"start": v(-72.12, -87.84) * mm, "end": v(-87.84, -103.55) * mm});
            skLineSegment(sketch, "E186", {"start": v(-87.84, -103.55) * mm, "end": v(-95.7, -95.7) * mm});
            skCircle(sketch, "E187", {"center": v(-87.84, 87.84) * mm, "radius": 3.3 * mm});
            skCircle(sketch, "E188", {"center": v(87.84, 87.84) * mm, "radius": 3.3 * mm});
            skCircle(sketch, "E189", {"center": v(124.22, 0) * mm, "radius": 3.3 * mm});
            skCircle(sketch, "E190", {"center": v(0, 124.22) * mm, "radius": 3.3 * mm});
            skCircle(sketch, "E191", {"center": v(87.84, -87.84) * mm, "radius": 3.3 * mm});
            skCircle(sketch, "E192", {"center": v(0, -124.22) * mm, "radius": 3.3 * mm});
            skCircle(sketch, "E193", {"center": v(-87.84, -87.84) * mm, "radius": 3.3 * mm});
            skCircle(sketch, "E194", {"center": v(-124.22, 0) * mm, "radius": 3.3 * mm});
            skCircle(sketch, "E195", {"center": v(0, 0) * mm, "radius": 41.78 * mm});
            skCircle(sketch, "E196", {"center": v(0, 0) * mm, "radius": 50.67 * mm});
            skCircle(sketch, "E197", {"center": v(0, 0) * mm, "radius": 44.32 * mm});
            skSolve(sketch);
        }
        {
            var Q0;
            Q0=makeQuery(id+"F7.imprint","IMPRINT",FACE,{"disambiguationData":[TD([[makeQuery(id+"F7.imprint","IMPRINT",EDGE,{"derivedFrom":sQuery(id+"F7.wireOp",EDGE,"E195")}),1.0]])]});
            var Q1;
            Q1=makeQuery(id+"F7.imprint","IMPRINT",FACE,{"disambiguationData":[TD([[makeQuery(id+"F7.imprint","IMPRINT",EDGE,{"derivedFrom":sQuery(id+"F7.wireOp",EDGE,"E195")}),-1.0]])]});
            extrude(context, id + "F8", {"entities" : qUnion([Q0, Q1]), "operationType" : NewBodyOperationType.REMOVE, "oppositeDirection" : true, "depth" : 25.4 * mm});
        }
        {
            var Q0;
            Q0=makeQuery(id+"F7.imprint","IMPRINT",FACE,{"disambiguationData":[TD([[makeQuery(id+"F7.imprint","IMPRINT",EDGE,{"derivedFrom":sQuery(id+"F7.wireOp",EDGE,"E195")}),-1.0]])]});
            var Q1;
            Q1=makeQuery(id+"F7.imprint","IMPRINT",FACE,{"disambiguationData":[TD([[makeQuery(id+"F7.imprint","IMPRINT",EDGE,{"derivedFrom":sQuery(id+"F7.wireOp",EDGE,"E196")}),1.0]])]});
            extrude(context, id + "F9", {"entities" : qUnion([Q0, Q1]), "oppositeDirection" : true, "depth" : 6.35 * mm});
        }
        {
            var Q0;
            Q0=makeQuery(id+"F7.imprint","IMPRINT",FACE,{"disambiguationData":[TD([[makeQuery(id+"F7.imprint","IMPRINT",EDGE,{"derivedFrom":sQuery(id+"F7.wireOp",EDGE,"E196")}),1.0]])]});
            extrude(context, id + "F10", {"entities" : qUnion([Q0]), "operationType" : NewBodyOperationType.REMOVE, "oppositeDirection" : true, "depth" : 6.35 * mm, "hasSecondDirection" : true, "secondDirectionOppositeDirection" : true, "secondDirectionDepth" : 3.17 * mm});
        }
        {
            var Q0;
            {var subQ1=sQuery(id+"F4.wireOp",EDGE,"E108");var subQ3=sQuery(id+"F4.wireOp",EDGE,"E137");var subQ4=makeQuery(id+"F4.imprint","INTERSECT",VERTEX,{"derivedFrom":[subQ1,subQ3]});Q0=makeQuery(id+"F4.imprint","IMPRINT",FACE,{"disambiguationData":[TD([[makeQuery(id+"F4.imprint","IMPRINT",EDGE,{"disambiguationData":[TD([[subQ4,-1.0]])],"derivedFrom":subQ3}),-1.0]])]});}
            var Q1;
            {var subQ1=sQuery(id+"F4.wireOp",EDGE,"E108");var subQ3=sQuery(id+"F4.wireOp",EDGE,"E138");var subQ4=makeQuery(id+"F4.imprint","INTERSECT",VERTEX,{"derivedFrom":[subQ1,subQ3]});Q1=makeQuery(id+"F4.imprint","IMPRINT",FACE,{"disambiguationData":[TD([[makeQuery(id+"F4.imprint","IMPRINT",EDGE,{"disambiguationData":[TD([[subQ4,-1.0]])],"derivedFrom":subQ3}),1.0]])]});}
            var Q2;
            {var subQ1=sQuery(id+"F4.wireOp",EDGE,"E112");var subQ3=sQuery(id+"F4.wireOp",EDGE,"E141");var subQ4=makeQuery(id+"F4.imprint","INTERSECT",VERTEX,{"derivedFrom":[subQ1,subQ3]});Q2=makeQuery(id+"F4.imprint","IMPRINT",FACE,{"disambiguationData":[TD([[makeQuery(id+"F4.imprint","IMPRINT",EDGE,{"disambiguationData":[TD([[subQ4,1.0]])],"derivedFrom":subQ3}),1.0]])]});}
            var Q3;
            {var subQ1=sQuery(id+"F4.wireOp",EDGE,"E112");var subQ3=sQuery(id+"F4.wireOp",EDGE,"E142");var subQ4=makeQuery(id+"F4.imprint","INTERSECT",VERTEX,{"derivedFrom":[subQ1,subQ3]});Q3=makeQuery(id+"F4.imprint","IMPRINT",FACE,{"disambiguationData":[TD([[makeQuery(id+"F4.imprint","IMPRINT",EDGE,{"disambiguationData":[TD([[subQ4,1.0]])],"derivedFrom":subQ3}),-1.0]])]});}
            var Q4;
            {var subQ1=sQuery(id+"F4.wireOp",EDGE,"E81");var subQ3=sQuery(id+"F4.wireOp",EDGE,"E135");var subQ4=makeQuery(id+"F4.imprint","INTERSECT",VERTEX,{"derivedFrom":[subQ1,subQ3]});Q4=makeQuery(id+"F4.imprint","IMPRINT",FACE,{"disambiguationData":[TD([[makeQuery(id+"F4.imprint","IMPRINT",EDGE,{"disambiguationData":[TD([[subQ4,1.0]])],"derivedFrom":subQ3}),1.0]])]});}
            var Q5;
            {var subQ1=sQuery(id+"F4.wireOp",EDGE,"E81");var subQ3=sQuery(id+"F4.wireOp",EDGE,"E136");var subQ4=makeQuery(id+"F4.imprint","INTERSECT",VERTEX,{"derivedFrom":[subQ1,subQ3]});Q5=makeQuery(id+"F4.imprint","IMPRINT",FACE,{"disambiguationData":[TD([[makeQuery(id+"F4.imprint","IMPRINT",EDGE,{"disambiguationData":[TD([[subQ4,1.0]])],"derivedFrom":subQ3}),-1.0]])]});}
            var Q6;
            {var subQ1=sQuery(id+"F4.wireOp",EDGE,"E85");var subQ3=sQuery(id+"F4.wireOp",EDGE,"E140");var subQ4=makeQuery(id+"F4.imprint","INTERSECT",VERTEX,{"derivedFrom":[subQ1,subQ3]});Q6=makeQuery(id+"F4.imprint","IMPRINT",FACE,{"disambiguationData":[TD([[makeQuery(id+"F4.imprint","IMPRINT",EDGE,{"disambiguationData":[TD([[subQ4,1.0]])],"derivedFrom":subQ3}),1.0]])]});}
            var Q7;
            {var subQ1=sQuery(id+"F4.wireOp",EDGE,"E85");var subQ3=sQuery(id+"F4.wireOp",EDGE,"E139");var subQ4=makeQuery(id+"F4.imprint","INTERSECT",VERTEX,{"derivedFrom":[subQ1,subQ3]});Q7=makeQuery(id+"F4.imprint","IMPRINT",FACE,{"disambiguationData":[TD([[makeQuery(id+"F4.imprint","IMPRINT",EDGE,{"disambiguationData":[TD([[subQ4,1.0]])],"derivedFrom":subQ3}),-1.0]])]});}
            var Q8;
            {var subQ1=sQuery(id+"F4.wireOp",EDGE,"E90");var subQ3=sQuery(id+"F4.wireOp",EDGE,"E138");var subQ4=makeQuery(id+"F4.imprint","INTERSECT",VERTEX,{"derivedFrom":[subQ1,subQ3]});Q8=makeQuery(id+"F4.imprint","IMPRINT",FACE,{"disambiguationData":[TD([[makeQuery(id+"F4.imprint","IMPRINT",EDGE,{"disambiguationData":[TD([[subQ4,1.0]])],"derivedFrom":subQ3}),1.0]])]});}
            var Q9;
            {var subQ1=sQuery(id+"F4.wireOp",EDGE,"E90");var subQ3=sQuery(id+"F4.wireOp",EDGE,"E137");var subQ4=makeQuery(id+"F4.imprint","INTERSECT",VERTEX,{"derivedFrom":[subQ1,subQ3]});Q9=makeQuery(id+"F4.imprint","IMPRINT",FACE,{"disambiguationData":[TD([[makeQuery(id+"F4.imprint","IMPRINT",EDGE,{"disambiguationData":[TD([[subQ4,1.0]])],"derivedFrom":subQ3}),-1.0]])]});}
            var Q10;
            {var subQ1=sQuery(id+"F4.wireOp",EDGE,"E94");var subQ3=sQuery(id+"F4.wireOp",EDGE,"E142");var subQ4=makeQuery(id+"F4.imprint","INTERSECT",VERTEX,{"derivedFrom":[subQ1,subQ3]});Q10=makeQuery(id+"F4.imprint","IMPRINT",FACE,{"disambiguationData":[TD([[makeQuery(id+"F4.imprint","IMPRINT",EDGE,{"disambiguationData":[TD([[subQ4,-1.0]])],"derivedFrom":subQ3}),-1.0]])]});}
            var Q11;
            {var subQ1=sQuery(id+"F4.wireOp",EDGE,"E94");var subQ3=sQuery(id+"F4.wireOp",EDGE,"E141");var subQ4=makeQuery(id+"F4.imprint","INTERSECT",VERTEX,{"derivedFrom":[subQ1,subQ3]});Q11=makeQuery(id+"F4.imprint","IMPRINT",FACE,{"disambiguationData":[TD([[makeQuery(id+"F4.imprint","IMPRINT",EDGE,{"disambiguationData":[TD([[subQ4,-1.0]])],"derivedFrom":subQ3}),1.0]])]});}
            var Q12;
            {var subQ1=sQuery(id+"F4.wireOp",EDGE,"E99");var subQ3=sQuery(id+"F4.wireOp",EDGE,"E136");var subQ4=makeQuery(id+"F4.imprint","INTERSECT",VERTEX,{"derivedFrom":[subQ1,subQ3]});Q12=makeQuery(id+"F4.imprint","IMPRINT",FACE,{"disambiguationData":[TD([[makeQuery(id+"F4.imprint","IMPRINT",EDGE,{"disambiguationData":[TD([[subQ4,-1.0]])],"derivedFrom":subQ3}),-1.0]])]});}
            var Q13;
            {var subQ1=sQuery(id+"F4.wireOp",EDGE,"E99");var subQ3=sQuery(id+"F4.wireOp",EDGE,"E135");var subQ4=makeQuery(id+"F4.imprint","INTERSECT",VERTEX,{"derivedFrom":[subQ1,subQ3]});Q13=makeQuery(id+"F4.imprint","IMPRINT",FACE,{"disambiguationData":[TD([[makeQuery(id+"F4.imprint","IMPRINT",EDGE,{"disambiguationData":[TD([[subQ4,-1.0]])],"derivedFrom":subQ3}),1.0]])]});}
            var Q14;
            {var subQ1=sQuery(id+"F4.wireOp",EDGE,"E103");var subQ3=sQuery(id+"F4.wireOp",EDGE,"E139");var subQ4=makeQuery(id+"F4.imprint","INTERSECT",VERTEX,{"derivedFrom":[subQ1,subQ3]});Q14=makeQuery(id+"F4.imprint","IMPRINT",FACE,{"disambiguationData":[TD([[makeQuery(id+"F4.imprint","IMPRINT",EDGE,{"disambiguationData":[TD([[subQ4,-1.0]])],"derivedFrom":subQ3}),-1.0]])]});}
            var Q15;
            {var subQ1=sQuery(id+"F4.wireOp",EDGE,"E103");var subQ3=sQuery(id+"F4.wireOp",EDGE,"E140");var subQ4=makeQuery(id+"F4.imprint","INTERSECT",VERTEX,{"derivedFrom":[subQ1,subQ3]});Q15=makeQuery(id+"F4.imprint","IMPRINT",FACE,{"disambiguationData":[TD([[makeQuery(id+"F4.imprint","IMPRINT",EDGE,{"disambiguationData":[TD([[subQ4,-1.0]])],"derivedFrom":subQ3}),1.0]])]});}
            extrude(context, id + "F11", {"entities" : qUnion([Q0, Q1, Q2, Q3, Q4, Q5, Q6, Q7, Q8, Q9, Q10, Q11, Q12, Q13, Q14, Q15]), "operationType" : NewBodyOperationType.REMOVE, "oppositeDirection" : true, "depth" : 3.17 * mm});
        }
        {
            var Q0;
            Q0=makeQuery(id+"F7.imprint","IMPRINT",FACE,{"disambiguationData":[TD([[makeQuery(id+"F7.imprint","IMPRINT",EDGE,{"derivedFrom":sQuery(id+"F7.wireOp",EDGE,"E160.bottom")}),1.0]])]});
            var Q1;
            Q1=makeQuery(id+"F7.imprint","IMPRINT",FACE,{"disambiguationData":[TD([[makeQuery(id+"F7.imprint","IMPRINT",EDGE,{"derivedFrom":sQuery(id+"F7.wireOp",EDGE,"E194")}),1.0]])]});
            var Q2;
            Q2=makeQuery(id+"F7.imprint","IMPRINT",FACE,{"disambiguationData":[TD([[makeQuery(id+"F7.imprint","IMPRINT",EDGE,{"derivedFrom":sQuery(id+"F7.wireOp",EDGE,"E182")}),-1.0]])]});
            var Q3;
            Q3=makeQuery(id+"F7.imprint","IMPRINT",FACE,{"disambiguationData":[TD([[makeQuery(id+"F7.imprint","IMPRINT",EDGE,{"derivedFrom":sQuery(id+"F7.wireOp",EDGE,"E193")}),1.0]])]});
            var Q4;
            Q4=makeQuery(id+"F7.imprint","IMPRINT",FACE,{"disambiguationData":[TD([[makeQuery(id+"F7.imprint","IMPRINT",EDGE,{"derivedFrom":sQuery(id+"F7.wireOp",EDGE,"E163.bottom")}),1.0]])]});
            var Q5;
            Q5=makeQuery(id+"F7.imprint","IMPRINT",FACE,{"disambiguationData":[TD([[makeQuery(id+"F7.imprint","IMPRINT",EDGE,{"derivedFrom":sQuery(id+"F7.wireOp",EDGE,"E192")}),1.0]])]});
            var Q6;
            Q6=makeQuery(id+"F7.imprint","IMPRINT",FACE,{"disambiguationData":[TD([[makeQuery(id+"F7.imprint","IMPRINT",EDGE,{"derivedFrom":sQuery(id+"F7.wireOp",EDGE,"E176")}),-1.0]])]});
            var Q7;
            Q7=makeQuery(id+"F7.imprint","IMPRINT",FACE,{"disambiguationData":[TD([[makeQuery(id+"F7.imprint","IMPRINT",EDGE,{"derivedFrom":sQuery(id+"F7.wireOp",EDGE,"E191")}),1.0]])]});
            var Q8;
            Q8=makeQuery(id+"F7.imprint","IMPRINT",FACE,{"disambiguationData":[TD([[makeQuery(id+"F7.imprint","IMPRINT",EDGE,{"derivedFrom":sQuery(id+"F7.wireOp",EDGE,"E189")}),1.0]])]});
            var Q9;
            Q9=makeQuery(id+"F7.imprint","IMPRINT",FACE,{"disambiguationData":[TD([[makeQuery(id+"F7.imprint","IMPRINT",EDGE,{"derivedFrom":sQuery(id+"F7.wireOp",EDGE,"E162.bottom")}),1.0]])]});
            var Q10;
            Q10=makeQuery(id+"F7.imprint","IMPRINT",FACE,{"disambiguationData":[TD([[makeQuery(id+"F7.imprint","IMPRINT",EDGE,{"derivedFrom":sQuery(id+"F7.wireOp",EDGE,"E188")}),1.0]])]});
            var Q11;
            Q11=makeQuery(id+"F7.imprint","IMPRINT",FACE,{"disambiguationData":[TD([[makeQuery(id+"F7.imprint","IMPRINT",EDGE,{"derivedFrom":sQuery(id+"F7.wireOp",EDGE,"E170")}),-1.0]])]});
            var Q12;
            Q12=makeQuery(id+"F7.imprint","IMPRINT",FACE,{"disambiguationData":[TD([[makeQuery(id+"F7.imprint","IMPRINT",EDGE,{"derivedFrom":sQuery(id+"F7.wireOp",EDGE,"E190")}),1.0]])]});
            var Q13;
            Q13=makeQuery(id+"F7.imprint","IMPRINT",FACE,{"disambiguationData":[TD([[makeQuery(id+"F7.imprint","IMPRINT",EDGE,{"derivedFrom":sQuery(id+"F7.wireOp",EDGE,"E161.bottom")}),-1.0]])]});
            var Q14;
            Q14=makeQuery(id+"F7.imprint","IMPRINT",FACE,{"disambiguationData":[TD([[makeQuery(id+"F7.imprint","IMPRINT",EDGE,{"derivedFrom":sQuery(id+"F7.wireOp",EDGE,"E187")}),1.0]])]});
            var Q15;
            {var subQ0=sQuery(id+"F7.wireOp",EDGE,"E165");Q15=makeQuery(id+"F7.imprint","IMPRINT",FACE,{"disambiguationData":[TD([[makeQuery(id+"F7.imprint","IMPRINT",EDGE,{"derivedFrom":subQ0}),-1.0]])]});}
            extrude(context, id + "F12", {"entities" : qUnion([Q0, Q1, Q2, Q3, Q4, Q5, Q6, Q7, Q8, Q9, Q10, Q11, Q12, Q13, Q14, Q15]), "operationType" : NewBodyOperationType.ADD, "oppositeDirection" : true, "depth" : 6.35 * mm});
        }
        {
            var Q0;
            Q0=makeQuery(id+"F7.imprint","IMPRINT",FACE,{"disambiguationData":[TD([[makeQuery(id+"F7.imprint","IMPRINT",EDGE,{"derivedFrom":sQuery(id+"F7.wireOp",EDGE,"E194")}),1.0]])]});
            var Q1;
            Q1=makeQuery(id+"F7.imprint","IMPRINT",FACE,{"disambiguationData":[TD([[makeQuery(id+"F7.imprint","IMPRINT",EDGE,{"derivedFrom":sQuery(id+"F7.wireOp",EDGE,"E187")}),1.0]])]});
            var Q2;
            Q2=makeQuery(id+"F7.imprint","IMPRINT",FACE,{"disambiguationData":[TD([[makeQuery(id+"F7.imprint","IMPRINT",EDGE,{"derivedFrom":sQuery(id+"F7.wireOp",EDGE,"E190")}),1.0]])]});
            var Q3;
            Q3=makeQuery(id+"F7.imprint","IMPRINT",FACE,{"disambiguationData":[TD([[makeQuery(id+"F7.imprint","IMPRINT",EDGE,{"derivedFrom":sQuery(id+"F7.wireOp",EDGE,"E188")}),1.0]])]});
            var Q4;
            Q4=makeQuery(id+"F7.imprint","IMPRINT",FACE,{"disambiguationData":[TD([[makeQuery(id+"F7.imprint","IMPRINT",EDGE,{"derivedFrom":sQuery(id+"F7.wireOp",EDGE,"E189")}),1.0]])]});
            var Q5;
            Q5=makeQuery(id+"F7.imprint","IMPRINT",FACE,{"disambiguationData":[TD([[makeQuery(id+"F7.imprint","IMPRINT",EDGE,{"derivedFrom":sQuery(id+"F7.wireOp",EDGE,"E191")}),1.0]])]});
            var Q6;
            Q6=makeQuery(id+"F7.imprint","IMPRINT",FACE,{"disambiguationData":[TD([[makeQuery(id+"F7.imprint","IMPRINT",EDGE,{"derivedFrom":sQuery(id+"F7.wireOp",EDGE,"E192")}),1.0]])]});
            var Q7;
            Q7=makeQuery(id+"F7.imprint","IMPRINT",FACE,{"disambiguationData":[TD([[makeQuery(id+"F7.imprint","IMPRINT",EDGE,{"derivedFrom":sQuery(id+"F7.wireOp",EDGE,"E193")}),1.0]])]});
            extrude(context, id + "F13", {"entities" : qUnion([Q0, Q1, Q2, Q3, Q4, Q5, Q6, Q7]), "operationType" : NewBodyOperationType.REMOVE, "oppositeDirection" : true, "depth" : 6.35 * mm, "hasSecondDirection" : true, "secondDirectionOppositeDirection" : true, "secondDirectionDepth" : 3.8 * mm});
        }
        {
            var Q0;
            Q0=qCreatedBy(makeId("Top.planeOp"),FACE);
            var sketch = newSketch(context, id + "F14", { "sketchPlane" : qUnion([Q0])});
            skCircle(sketch, "E198", {"center": v(0, 0) * mm, "radius": 3.05 * mm});
            skCircle(sketch, "E199", {"center": v(0, 0) * mm, "radius": 5.59 * mm});
            skSolve(sketch);
        }
        {
            var Q0;
            Q0 = qSketchRegion(id + "F14", true);
            var Q1;
            Q1=makeQuery(id+"F14.imprint","IMPRINT",FACE,{"disambiguationData":[TD([[makeQuery(id+"F14.imprint","IMPRINT",EDGE,{"derivedFrom":sQuery(id+"F14.wireOp",EDGE,"E198")}),1.0]])]});
            extrude(context, id + "F15", {"entities" : qUnion([Q0, Q1]), "oppositeDirection" : true, "depth" : 50.8 * mm});
        }
        {
            var Q0;
            Q0=qCreatedBy(makeId("Front.planeOp"),FACE);
            var sketch = newSketch(context, id + "F16", { "sketchPlane" : qUnion([Q0])});
            skLineSegment(sketch, "E200", {"start": v(0, 0) * mm, "end": v(-3.05, 0) * mm, "construction": true});
            skLineSegment(sketch, "E201", {"start": v(-3.05, 0) * mm, "end": v(-3.05, -17.4) * mm, "construction": true});
            skLineSegment(sketch, "E202", {"start": v(-3.05, -17.4) * mm, "end": v(-27.6, 7.14) * mm});
            skLineSegment(sketch, "E203", {"start": v(-27.6, 7.14) * mm, "end": v(-27.6, -52.88) * mm});
            skLineSegment(sketch, "E204", {"start": v(-27.6, -52.88) * mm, "end": v(32.43, -52.88) * mm});
            skLineSegment(sketch, "E205", {"start": v(32.43, -52.88) * mm, "end": v(-3.05, -17.4) * mm});
            skSolve(sketch);
        }
        {
            var Q0;
            Q0 = qSketchRegion(id + "F16", true);
            extrude(context, id + "F17", {"entities" : qUnion([Q0]), "operationType" : NewBodyOperationType.REMOVE, "oppositeDirection" : true, "depth" : 25.4 * mm, "hasSecondDirection" : true, "secondDirectionOppositeDirection" : false, "secondDirectionDepth" : 25.4 * mm});
        }
        {
            var Q0;
            Q0=makeQuery(id+"F14.imprint","IMPRINT",FACE,{"disambiguationData":[TD([[makeQuery(id+"F14.imprint","IMPRINT",EDGE,{"derivedFrom":sQuery(id+"F14.wireOp",EDGE,"E198")}),1.0]])]});
            extrude(context, id + "F18", {"entities" : qUnion([Q0]), "operationType" : NewBodyOperationType.ADD, "depth" : 2.54 * mm, "hasSecondDirection" : true, "secondDirectionOppositeDirection" : true, "secondDirectionDepth" : 5.08 * mm});
        }
    });
